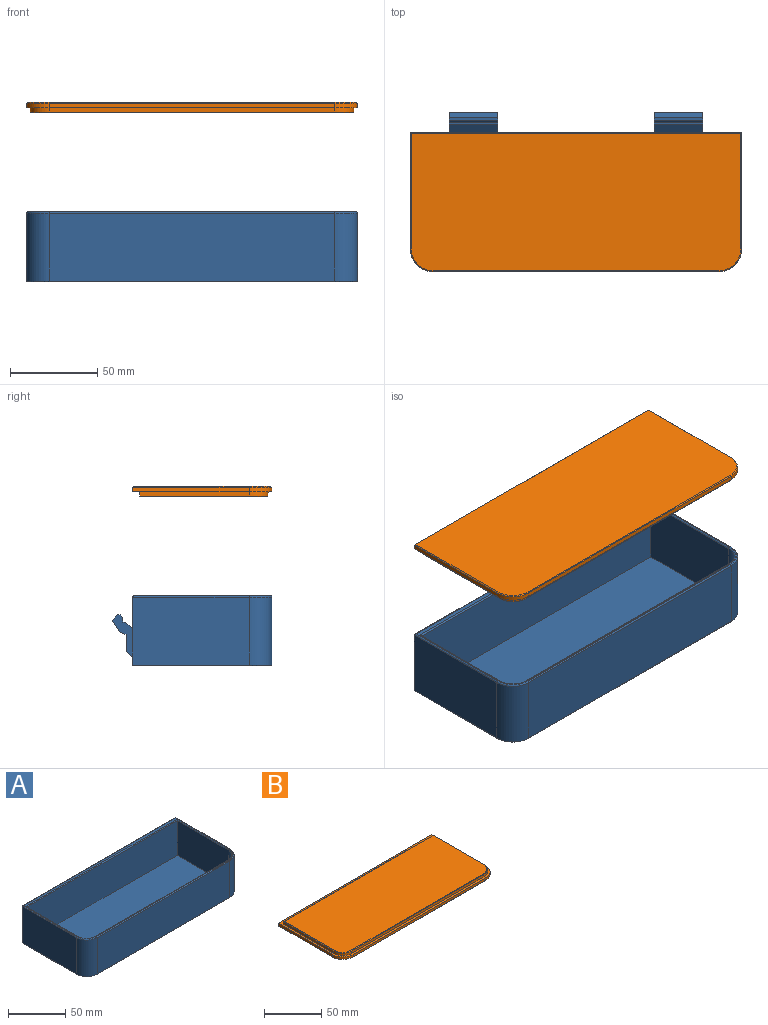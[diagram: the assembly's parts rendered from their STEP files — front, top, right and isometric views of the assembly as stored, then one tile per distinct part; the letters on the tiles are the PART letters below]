
ASSEMBLY  parts=2 mates=1
PART A: 57 faces, bbox 192.1x92.7x40 mm
  f0: plane 190x39mm, normal (0,1,0), area 6484mm2, adj f2,f4,f17,f18,f23,f24,f28,f29
  f1: plane 188.5x78.5mm, normal (0,0,1), area 635.8mm2, adj f39,f40,f41,f42,f43,f44,f45,f46
  f2: plane 67x39mm, normal (-1,0,0), area 2613mm2, adj f0,f12,f48,f52
  f3: plane 164x39mm, normal (0,-1,0), area 6396mm2, adj f12,f13,f49,f53
  f4: plane 67x39mm, normal (1,0,0), area 2613mm2, adj f0,f13,f45,f56
  f5: plane 189.5x79.5mm, normal (0,0,-1), area 14995.5mm2, adj f51,f52,f53,f54,f55,f56
  f6: plane 63x37.25mm, normal (1,0,0), area 2346.7mm2, adj f9,f11,f36,f42
  f7: plane 164x37.25mm, normal (0,1,0), area 6109mm2, adj f9,f10,f11,f39
  f8: plane 63x37.25mm, normal (-1,0,0), area 2346.7mm2, adj f9,f10,f36,f43
  f9: plane 186x74mm, normal (0,0,1), area 13712.1mm2, adj f6,f7,f8,f10,f11,f36
  f10: cylinder r=11mm len=37.25mm, axis (0,0,-1), area 643.6mm2, adj f7,f8,f9,f41
  f11: cylinder r=11mm len=37.25mm, axis (0,0,1), area 643.6mm2, adj f6,f7,f9,f40
  f12: cylinder r=13mm len=39mm, axis (0,0,-1), area 796.4mm2, adj f2,f3,f50,f51
  f13: cylinder r=13mm len=39mm, axis (0,0,1), area 796.4mm2, adj f3,f4,f47,f55
  f14: plane 27.7x1.48mm, normal (0,0,1), area 41mm2, adj f22,f23,f24,f37
  f15: plane 27.7x2.65mm, normal (0,-1,0), area 73.4mm2, adj f16,f23,f24,f37
  f16: plane 27.7x1.01mm, normal (0,0,1), area 28mm2, adj f15,f17,f23,f24
  f17: plane 27.7x4.57mm, normal (0,-0.59,0.81), area 157.1mm2, adj f0,f16,f23,f24
  f18: plane 27.7x3.68mm, normal (0,0.63,-0.78), area 130.6mm2, adj f0,f19,f23,f24
  f19: plane 27.7x10mm, normal (0,1,0), area 277mm2, adj f18,f20,f23,f24
  f20: plane 27.7x3.37mm, normal (0,0.32,-0.95), area 98.3mm2, adj f19,f21,f23,f24
  f21: plane 27.7x7.02mm, normal (0,0.83,-0.55), area 233mm2, adj f20,f22,f23,f24
  f22: plane 27.7x3.12mm, normal (0,0.71,0.71), area 122.2mm2, adj f14,f21,f23,f24
  f23: plane 24.22x11.68mm, normal (-1,0,0), area 113.6mm2, adj f0,f14,f15,f16,f17,f18,f19,f20
  f24: plane 24.22x11.68mm, normal (1,0,0), area 113.6mm2, adj f0,f14,f15,f16,f17,f18,f19,f20
  f25: plane 27.7x1.48mm, normal (0,0,1), area 41mm2, adj f33,f34,f35,f38
  f26: plane 27.7x2.65mm, normal (0,-1,0), area 73.4mm2, adj f27,f34,f35,f38
  f27: plane 27.7x1.01mm, normal (0,0,1), area 28mm2, adj f26,f28,f34,f35
  f28: plane 27.7x4.57mm, normal (0,-0.59,0.81), area 157.1mm2, adj f0,f27,f34,f35
  f29: plane 27.7x3.68mm, normal (0,0.63,-0.78), area 130.6mm2, adj f0,f30,f34,f35
  f30: plane 27.7x10mm, normal (0,1,0), area 277mm2, adj f29,f31,f34,f35
  f31: plane 27.7x3.37mm, normal (0,0.32,-0.95), area 98.3mm2, adj f30,f32,f34,f35
  f32: plane 27.7x7.02mm, normal (0,0.83,-0.55), area 233mm2, adj f31,f33,f34,f35
  f33: plane 27.7x3.12mm, normal (0,0.71,0.71), area 122.2mm2, adj f25,f32,f34,f35
  f34: plane 24.22x11.68mm, normal (1,0,0), area 113.6mm2, adj f0,f25,f26,f27,f28,f29,f30,f31
  f35: plane 24.22x11.68mm, normal (-1,0,0), area 113.6mm2, adj f0,f25,f26,f27,f28,f29,f30,f31
  f36: plane 186x37.25mm, normal (0,-1,0), area 6928.5mm2, adj f6,f8,f9,f44
  f37: plane 27.7x1.5mm, normal (0,-0.71,0.71), area 58.8mm2, adj f14,f15,f23,f24
  f38: plane 27.7x1.5mm, normal (0,-0.71,0.71), area 58.8mm2, adj f25,f26,f34,f35
  f39: cylinder r=0.75mm len=164mm, axis (1,0,0), area 193.2mm2, adj f1,f7,f40,f41
  f40: torus R=11.75mm, axis (0,0,1), area 20.9mm2, adj f1,f11,f39,f42
  f41: torus R=11.75mm, axis (0,0,1), area 20.9mm2, adj f1,f10,f39,f43
  f42: cylinder r=0.75mm len=63.75mm, axis (0,-1,0), area 74.5mm2, adj f1,f6,f40,f44
  f43: cylinder r=0.75mm len=63.75mm, axis (0,1,0), area 74.5mm2, adj f1,f8,f41,f44
  f44: cylinder r=0.75mm len=187.5mm, axis (-1,0,0), area 219.8mm2, adj f1,f36,f42,f43
  f45: cylinder r=0.75mm len=67mm, axis (0,-1,0), area 78.6mm2, adj f1,f4,f46,f47
  f46: cylinder r=0.75mm len=190mm, axis (1,0,0), area 223.2mm2, adj f0,f1,f45,f48
  f47: torus R=12.25mm, axis (0,0,1), area 23.6mm2, adj f1,f13,f45,f49
  f48: cylinder r=0.75mm len=67mm, axis (0,1,0), area 78.6mm2, adj f1,f2,f46,f50
  f49: cylinder r=0.75mm len=164mm, axis (-1,0,0), area 193.2mm2, adj f1,f3,f47,f50
  f50: torus R=12.25mm, axis (0,0,1), area 23.6mm2, adj f1,f12,f48,f49
  f51: cone r=12.75mm half-angle=45deg, axis (0,0,1), area 7.2mm2, adj f5,f12,f52,f53
  f52: plane 67x0.25mm, normal (-0.71,0,-0.71), area 23.6mm2, adj f2,f5,f51,f54
  f53: plane 164x0.25mm, normal (0,-0.71,-0.71), area 58mm2, adj f3,f5,f51,f55
  f54: plane 190x0.25mm, normal (0,0.71,-0.71), area 67.1mm2, adj f0,f5,f52,f56
  f55: cone r=12.75mm half-angle=45deg, axis (0,0,1), area 7.2mm2, adj f5,f13,f53,f56
  f56: plane 67x0.25mm, normal (0.71,0,-0.71), area 23.6mm2, adj f4,f5,f54,f55
PART B: 27 faces, bbox 190x80x6 mm
  f0: plane 190x80mm, normal (0,0,1), area 1504.4mm2, adj f1,f2,f3,f4,f6,f7,f9,f10
  f1: plane 190x2.5mm, normal (0,1,0), area 475mm2, adj f0,f2,f4,f24
  f2: plane 67x2.5mm, normal (-1,0,0), area 167.5mm2, adj f0,f1,f6,f22
  f3: plane 164x2.5mm, normal (0,-1,0), area 410mm2, adj f0,f6,f7,f23
  f4: plane 67x2.5mm, normal (1,0,0), area 167.5mm2, adj f0,f1,f7,f26
  f5: plane 189x79mm, normal (0,0,-1), area 14863.9mm2, adj f21,f22,f23,f24,f25,f26
  f6: cylinder r=13mm len=13mm, axis (0,0,1), area 51.1mm2, adj f0,f2,f3,f21
  f7: cylinder r=13mm len=13mm, axis (0,0,-1), area 51.1mm2, adj f0,f3,f4,f25
  f8: plane 184.48x72.48mm, normal (0,0,1), area 13325mm2, adj f15,f16,f17,f18,f19,f20
  f9: plane 164x2.52mm, normal (0,-1,0.03), area 413.1mm2, adj f0,f10,f11,f15
  f10: cone r=10.72mm half-angle=2deg, axis (0,0,-1), area 42.7mm2, adj f0,f9,f12,f17
  f11: cone r=10.72mm half-angle=2deg, axis (0,0,-1), area 42.7mm2, adj f0,f9,f13,f16
  f12: plane 62.83x2.52mm, normal (-1,0,0.03), area 158.1mm2, adj f0,f10,f14,f19
  f13: plane 62.83x2.52mm, normal (1,0,0.03), area 158.1mm2, adj f0,f11,f14,f18
  f14: plane 185.65x2.52mm, normal (0,1,0.03), area 467.4mm2, adj f0,f12,f13,f20
  f15: plane 164x0.5mm, normal (0,-0.69,0.72), area 113.9mm2, adj f8,f9,f16,f17
  f16: cone r=10.24mm half-angle=46deg, axis (0,0,-1), area 11.4mm2, adj f8,f11,f15,f18
  f17: cone r=10.24mm half-angle=46deg, axis (0,0,-1), area 11.4mm2, adj f8,f10,f15,f19
  f18: plane 62.74x0.5mm, normal (0.69,0,0.72), area 43.4mm2, adj f8,f13,f16,f20
  f19: plane 62.74x0.5mm, normal (-0.69,0,0.72), area 43.4mm2, adj f8,f12,f17,f20
  f20: plane 185.48x0.5mm, normal (0,0.69,0.72), area 128.5mm2, adj f8,f14,f18,f19
  f21: cone r=12.5mm half-angle=45deg, axis (0,0,1), area 14.2mm2, adj f5,f6,f22,f23
  f22: plane 67x0.5mm, normal (-0.71,0,-0.71), area 47.2mm2, adj f2,f5,f21,f24
  f23: plane 164x0.5mm, normal (0,-0.71,-0.71), area 116mm2, adj f3,f5,f21,f25
  f24: plane 190x0.5mm, normal (0,0.71,-0.71), area 134mm2, adj f1,f5,f22,f26
  f25: cone r=12.5mm half-angle=45deg, axis (0,0,1), area 14.2mm2, adj f5,f7,f23,f26
  f26: plane 67x0.5mm, normal (0.71,0,-0.71), area 47.2mm2, adj f4,f5,f24,f25
PLACE A t=(-20.93,-2.14,3.67)mm fixed
PLACE B rot(axis=(0,1,0),180deg) t=(-20.93,-2.13,6.52)mm
MATE slider A.f9 <-> B.f8  axis (0,0,1) through (-20.93,-3.01,5.67)mm
